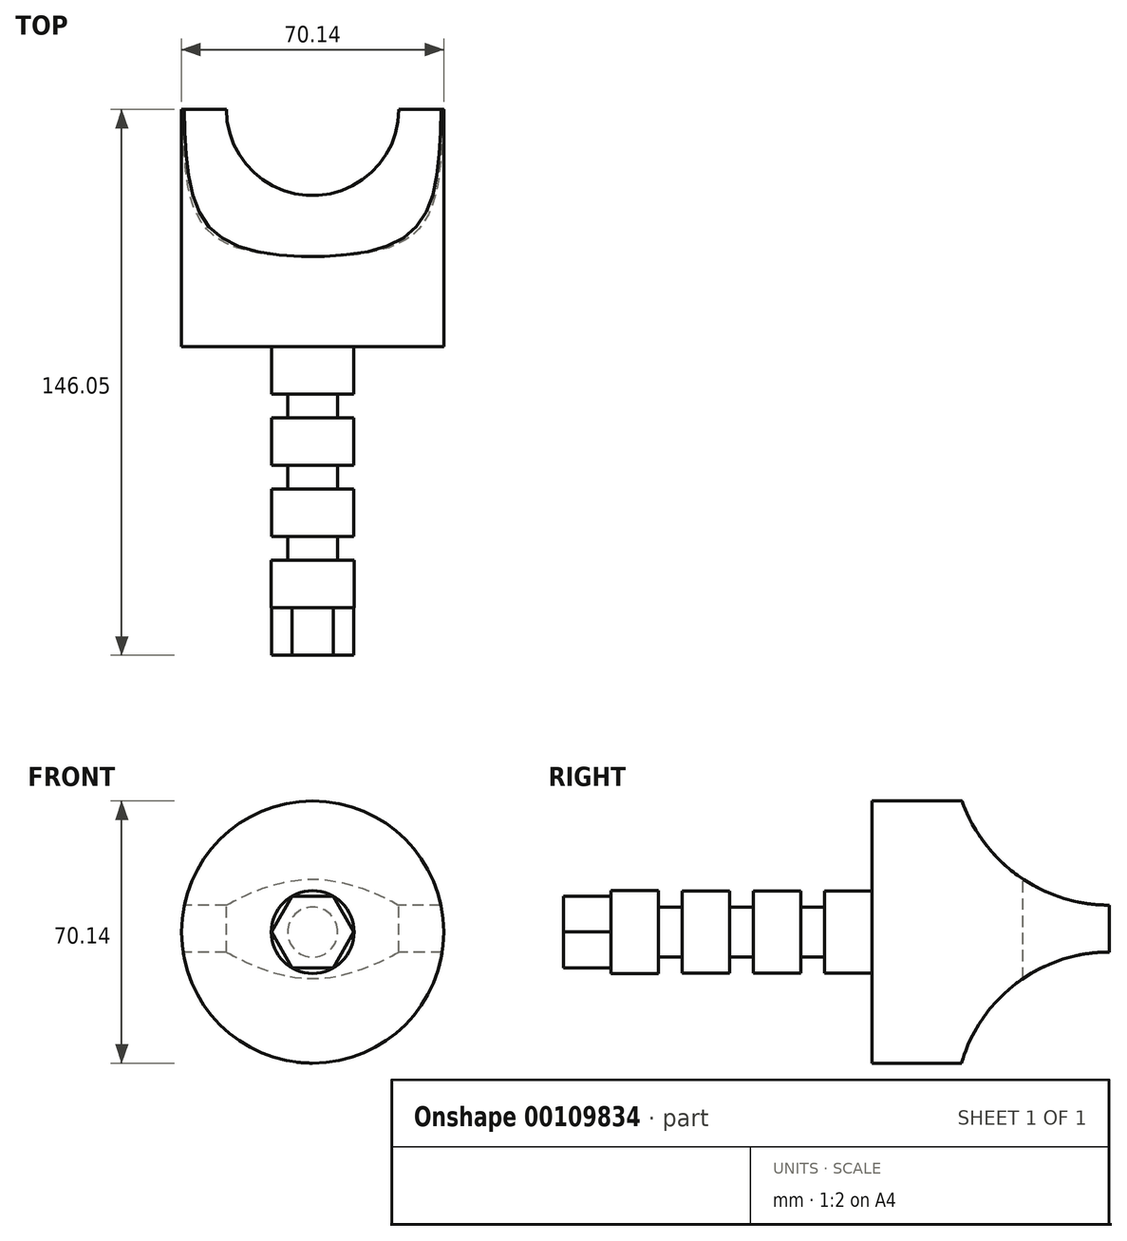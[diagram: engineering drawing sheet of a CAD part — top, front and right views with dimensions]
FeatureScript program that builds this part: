
annotation { "Feature Type Name" : "Feature", "Feature Type Description" : "" }
export const myFeature = defineFeature(function(context is Context, id is Id, definition is map)
    precondition{}
    {
        {
            var Q0;
            Q0=qCreatedBy(makeId("Front.planeOp"),FACE);
            var sketch = newSketch(context, id + "F0", { "sketchPlane" : qUnion([Q0])});
            skCircle(sketch, "E0", {"center": v(0, 0) * mm, "radius": 35.07 * mm});
            skSolve(sketch);
        }
        {
            var Q0;
            Q0 = qSketchRegion(id + "F0", true);
            extrude(context, id + "F1", {"entities" : qUnion([Q0]), "oppositeDirection" : true, "depth" : 63.5 * mm});
        }
        {
            var Q0;
            Q0=makeQuery(id+"F1.opExtrude","CAP_FACE",FACE,{"disambiguationData":[OSD([sQuery(id+"F0.wireOp",EDGE,"E0")])],"isStart":true});
            var sketch = newSketch(context, id + "F2", { "sketchPlane" : qUnion([Q0])});
            skCircle(sketch, "E1", {"center": v(0, 0) * mm, "radius": 11.02 * mm});
            skSolve(sketch);
        }
        {
            var Q0;
            Q0 = qSketchRegion(id + "F2", true);
            extrude(context, id + "F3", {"entities" : qUnion([Q0]), "operationType" : NewBodyOperationType.ADD, "depth" : 12.7 * mm});
        }
        {
            var Q0;
            Q0=makeQuery(id+"F3.opExtrude","CAP_FACE",FACE,{"disambiguationData":[OSD([sQuery(id+"F2.wireOp",EDGE,"E1")])],"isStart":false});
            var sketch = newSketch(context, id + "F4", { "sketchPlane" : qUnion([Q0])});
            skCircle(sketch, "E2", {"center": v(0, 0) * mm, "radius": 6.69 * mm});
            skSolve(sketch);
        }
        {
            var Q0;
            Q0 = qSketchRegion(id + "F4", true);
            extrude(context, id + "F5", {"entities" : qUnion([Q0]), "operationType" : NewBodyOperationType.ADD, "depth" : 69.85 * mm});
        }
        {
            var Q0;
            Q0=makeQuery(id+"F3.opExtrude","CAP_FACE",FACE,{"disambiguationData":[OSD([sQuery(id+"F2.wireOp",EDGE,"E1")])],"isStart":false});
            var sketch = newSketch(context, id + "F6", { "sketchPlane" : qUnion([Q0])});
            skCircle(sketch, "E3.cCircle", {"center": v(0, 0) * mm, "radius": 11.02 * mm, "construction": true});
            skLineSegment(sketch, "E3.0", {"start": v(5.5, -9.54) * mm, "end": v(-5.5, -9.54) * mm});
            skLineSegment(sketch, "E3.1", {"start": v(-5.5, -9.54) * mm, "end": v(-11.02, 0) * mm});
            skLineSegment(sketch, "E3.2", {"start": v(-11.02, 0) * mm, "end": v(-5.5, 9.54) * mm});
            skLineSegment(sketch, "E3.3", {"start": v(-5.5, 9.54) * mm, "end": v(5.5, 9.54) * mm});
            skLineSegment(sketch, "E3.4", {"start": v(5.5, 9.54) * mm, "end": v(11.02, 0) * mm});
            skLineSegment(sketch, "E3.5", {"start": v(11.02, 0) * mm, "end": v(5.5, -9.54) * mm});
            skSolve(sketch);
        }
        {
            var Q0;
            Q0 = qSketchRegion(id + "F6", true);
            extrude(context, id + "F7", {"entities" : qUnion([Q0]), "operationType" : NewBodyOperationType.ADD, "depth" : 69.85 * mm, "hasSecondDirection" : true, "secondDirectionOppositeDirection" : false, "secondDirectionDepth" : 50.8 * mm});
        }
        {
            var Q0;
            Q0=makeQuery(id+"F3.opExtrude","CAP_FACE",FACE,{"disambiguationData":[OSD([sQuery(id+"F2.wireOp",EDGE,"E1")])],"isStart":false});
            var sketch = newSketch(context, id + "F8", { "sketchPlane" : qUnion([Q0])});
            skCircle(sketch, "E4", {"center": v(0, 0) * mm, "radius": 11.03 * mm});
            skSolve(sketch);
        }
        {
            var Q0;
            Q0 = qSketchRegion(id + "F8", true);
            extrude(context, id + "F9", {"entities" : qUnion([Q0]), "operationType" : NewBodyOperationType.ADD, "depth" : 19.05 * mm, "hasSecondDirection" : true, "secondDirectionOppositeDirection" : false, "secondDirectionDepth" : 6.35 * mm});
        }
        {
            var Q0;
            Q0=makeQuery(id+"F9.opExtrude","CAP_FACE",FACE,{"disambiguationData":[OSD([sQuery(id+"F8.wireOp",EDGE,"E4")])],"isStart":false});
            var sketch = newSketch(context, id + "F10", { "sketchPlane" : qUnion([Q0])});
            skCircle(sketch, "E5", {"center": v(0, 0) * mm, "radius": 11.01 * mm});
            skSolve(sketch);
        }
        {
            var Q0;
            Q0 = qSketchRegion(id + "F10", true);
            extrude(context, id + "F11", {"entities" : qUnion([Q0]), "operationType" : NewBodyOperationType.ADD, "depth" : 19.05 * mm, "hasSecondDirection" : true, "secondDirectionOppositeDirection" : false, "secondDirectionDepth" : 6.35 * mm});
        }
        {
            var Q0;
            Q0=makeQuery(id+"F11.opExtrude","CAP_FACE",FACE,{"disambiguationData":[OSD([sQuery(id+"F10.wireOp",EDGE,"E5")])],"isStart":false});
            var sketch = newSketch(context, id + "F12", { "sketchPlane" : qUnion([Q0])});
            skCircle(sketch, "E6", {"center": v(0, 0) * mm, "radius": 11.07 * mm});
            skSolve(sketch);
        }
        {
            var Q0;
            Q0 = qSketchRegion(id + "F12", true);
            extrude(context, id + "F13", {"entities" : qUnion([Q0]), "operationType" : NewBodyOperationType.ADD, "depth" : 19.05 * mm, "hasSecondDirection" : true, "secondDirectionOppositeDirection" : false, "secondDirectionDepth" : 6.35 * mm});
        }
        {
            var Q0;
            Q0=makeQuery(id+"F1.opExtrude","CAP_FACE",FACE,{"disambiguationData":[OSD([sQuery(id+"F0.wireOp",EDGE,"E0")])],"isStart":false});
            var sketch = newSketch(context, id + "F14", { "sketchPlane" : qUnion([Q0])});
            skLineSegment(sketch, "E7.bottom", {"start": v(34.66, -5.35) * mm, "end": v(18.5, -5.35) * mm});
            skLineSegment(sketch, "E7.top", {"start": v(34.66, 5.35) * mm, "end": v(18.5, 5.35) * mm});
            skLineSegment(sketch, "E7.left", {"start": v(34.66, -5.35) * mm, "end": v(34.66, 5.35) * mm});
            skLineSegment(sketch, "E7.right", {"start": v(18.5, -5.35) * mm, "end": v(18.5, 5.35) * mm});
            skPoint(sketch, "E7.middle", {"position": v(26.58, 0) * mm});
            skLineSegment(sketch, "E8.MirrorCS", {"start": v(-18.5, -5.35) * mm, "end": v(-18.5, 5.35) * mm});
            skLineSegment(sketch, "E9.MirrorCS", {"start": v(-34.66, -5.35) * mm, "end": v(-18.5, -5.35) * mm});
            skLineSegment(sketch, "E10.MirrorCS", {"start": v(-34.66, 5.35) * mm, "end": v(-18.5, 5.35) * mm});
            skLineSegment(sketch, "E11.MirrorCS", {"start": v(-34.66, -5.35) * mm, "end": v(-34.66, 5.35) * mm});
            skLineSegment(sketch, "E12", {"start": v(-34.66, -5.35) * mm, "end": v(34.66, -5.35) * mm});
            skArc(sketch, "E13", {"start": v(-34.66, -5.35) * mm, "mid": v(0, -40) * mm, "end": v(34.66, -5.35) * mm});
            skLineSegment(sketch, "E14", {"start": v(-50.1, -46.43) * mm, "end": v(54.74, -46.43) * mm, "construction": true});
            skSolve(sketch);
        }
        {
            var Q0;
            {var subQ0=sQuery(id+"F14.wireOp",EDGE,"E12");var subQ5=makeQuery(id+"F14.imprint","INTERSECT",VERTEX,{"derivedFrom":[sQuery(id+"F14.wireOp",EDGE,"E7.right"),subQ0]});Q0=makeQuery(id+"F14.imprint","IMPRINT",FACE,{"disambiguationData":[TD([[makeQuery(id+"F14.imprint","IMPRINT",EDGE,{"disambiguationData":[TD([[subQ5,1.0]])],"derivedFrom":subQ0}),-1.0]])]});}
            var Q1;
            Q1=sQuery(id+"F14.wireOp",EDGE,"E14");
            revolve(context, id + "F15", {"operationType" : NewBodyOperationType.REMOVE, "entities" : qUnion([Q0]), "axis" : qUnion([Q1]), "revolveType" : RevolveType.FULL, "oppositeDirection" : true});
        }
        {
            var Q0;
            Q0=makeQuery(id+"F1.opExtrude","CAP_FACE",FACE,{"disambiguationData":[OSD([sQuery(id+"F0.wireOp",EDGE,"E0")])],"isStart":false});
            var sketch = newSketch(context, id + "F16", { "sketchPlane" : qUnion([Q0])});
            skLineSegment(sketch, "E15", {"start": v(-34.32, 7.21) * mm, "end": v(34.32, 7.21) * mm});
            skArc(sketch, "E16", {"start": v(34.32, 7.21) * mm, "mid": v(0, 40.56) * mm, "end": v(-34.32, 7.21) * mm});
            skLineSegment(sketch, "E17", {"start": v(-37.2, 48.9) * mm, "end": v(57.03, 48.9) * mm, "construction": true});
            skSolve(sketch);
        }
        {
            var Q0;
            Q0 = qSketchRegion(id + "F16", true);
            var Q1;
            Q1=sQuery(id+"F16.wireOp",EDGE,"E17");
            revolve(context, id + "F17", {"operationType" : NewBodyOperationType.REMOVE, "entities" : qUnion([Q0]), "axis" : qUnion([Q1]), "revolveType" : RevolveType.FULL, "oppositeDirection" : true});
        }
        {
            var Q0;
            Q0=qCreatedBy(makeId("Top.planeOp"),FACE);
            var sketch = newSketch(context, id + "F18", { "sketchPlane" : qUnion([Q0])});
            skCircle(sketch, "E18", {"center": v(0, 63.56) * mm, "radius": 23.09 * mm});
            skSolve(sketch);
        }
        {
            var Q0;
            Q0 = qSketchRegion(id + "F18", true);
            extrude(context, id + "F19", {"entities" : qUnion([Q0]), "operationType" : NewBodyOperationType.REMOVE, "endBound" : BoundingType.SYMMETRIC, "oppositeDirection" : true, "depth" : 127 * mm});
        }
    });
